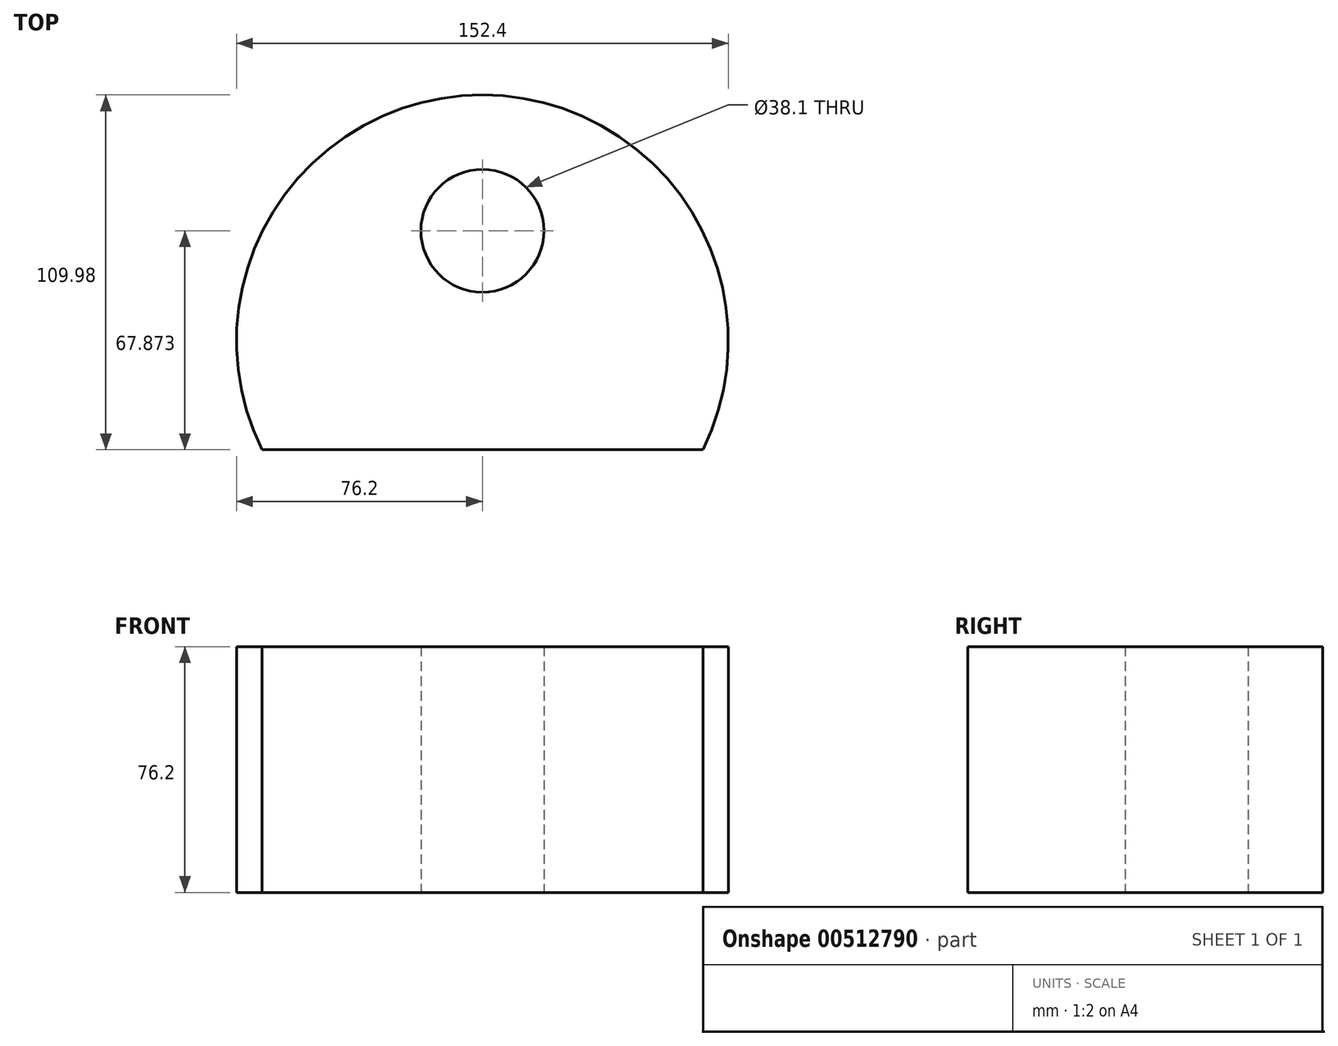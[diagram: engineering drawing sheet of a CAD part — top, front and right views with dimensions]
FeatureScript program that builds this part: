
annotation { "Feature Type Name" : "Feature", "Feature Type Description" : "" }
export const myFeature = defineFeature(function(context is Context, id is Id, definition is map)
    precondition{}
    {
        {
            var Q0;
            Q0=qCreatedBy(makeId("Top.planeOp"),FACE);
            var sketch = newSketch(context, id + "F0", { "sketchPlane" : qUnion([Q0])});
            skArc(sketch, "E0", {"start": v(68.3, -33.78) * mm, "mid": v(0, 76.2) * mm, "end": v(-68.3, -33.78) * mm});
            skLineSegment(sketch, "E1", {"start": v(-68.3, -33.78) * mm, "end": v(68.3, -33.78) * mm});
            skSolve(sketch);
        }
        {
            var Q0;
            Q0=qSketchRegion(id+"F0",true);
            extrude(context, id + "F1", {"entities" : qUnion([Q0]), "depth" : 76.2 * mm});
        }
        {
            var Q0;
            Q0=qCreatedBy(makeId("Top.planeOp"),FACE);
            var sketch = newSketch(context, id + "F2", { "sketchPlane" : qUnion([Q0])});
            skCircle(sketch, "E2", {"center": v(0, 34.1) * mm, "radius": 19.05 * mm});
            skSolve(sketch);
        }
        {
            var Q0;
            Q0=qSketchRegion(id+"F2",true);
            extrude(context, id + "F3", {"entities" : qUnion([Q0]), "operationType" : NewBodyOperationType.REMOVE, "endBound" : BoundingType.THROUGH_ALL, "depth" : 25.4 * mm});
        }
    });
